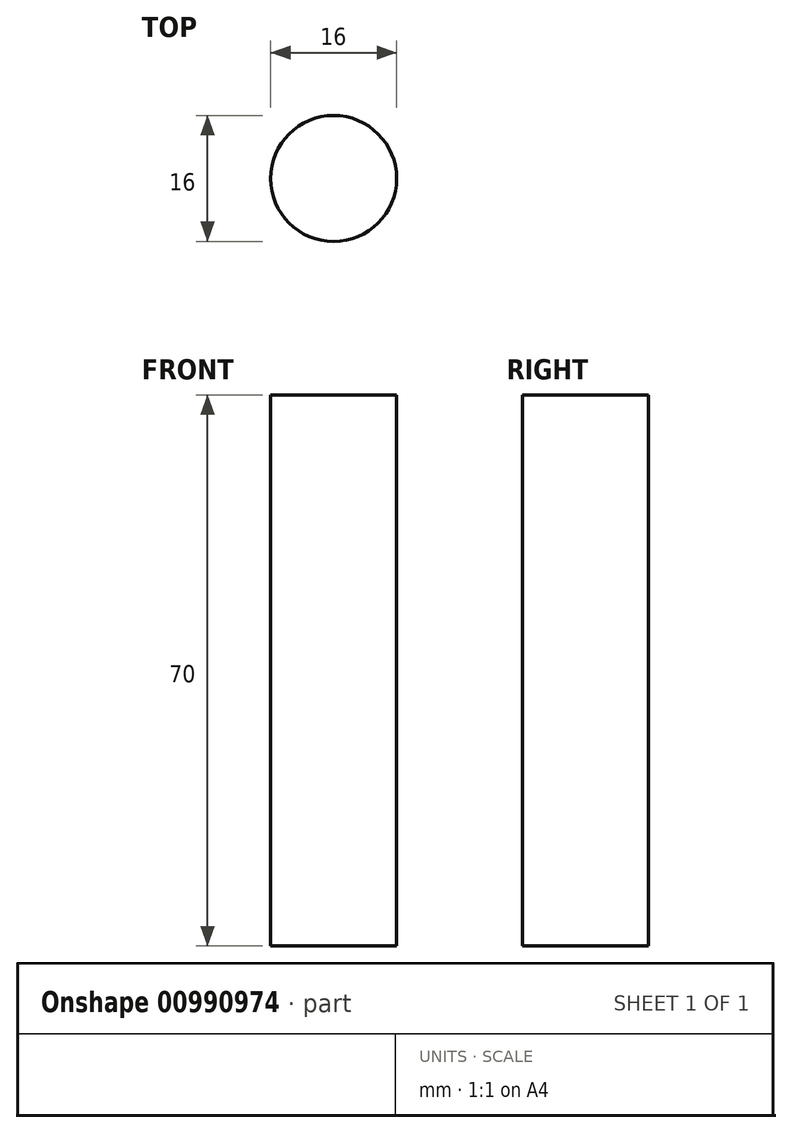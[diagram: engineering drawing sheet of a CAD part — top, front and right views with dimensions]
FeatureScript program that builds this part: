
annotation { "Feature Type Name" : "Feature", "Feature Type Description" : "" }
export const myFeature = defineFeature(function(context is Context, id is Id, definition is map)
    precondition{}
    {
        {
            var Q0;
            Q0=qCreatedBy(makeId("Top.planeOp"),FACE);
            var sketch = newSketch(context, id + "F0", { "sketchPlane" : qUnion([Q0])});
            skCircle(sketch, "E0", {"center": v(0, 0) * mm, "radius": 8 * mm});
            skSolve(sketch);
        }
        {
            var Q0;
            Q0=makeQuery(id+"F0.imprint","IMPRINT",FACE,{"disambiguationData":[TD([[makeQuery(id+"F0.imprint","IMPRINT",EDGE,{"derivedFrom":sQuery(id+"F0.wireOp",EDGE,"E0")}),1.0]])]});
            var Q1;
            Q1=sQuery(id+"F0.wireOp",EDGE,"E0");
            extrude(context, id + "F1", {"entities" : qUnion([Q0]), "surfaceEntities" : qUnion([Q1]), "depth" : 70 * mm, "offsetDistance" : 25 * mm});
        }
    });
